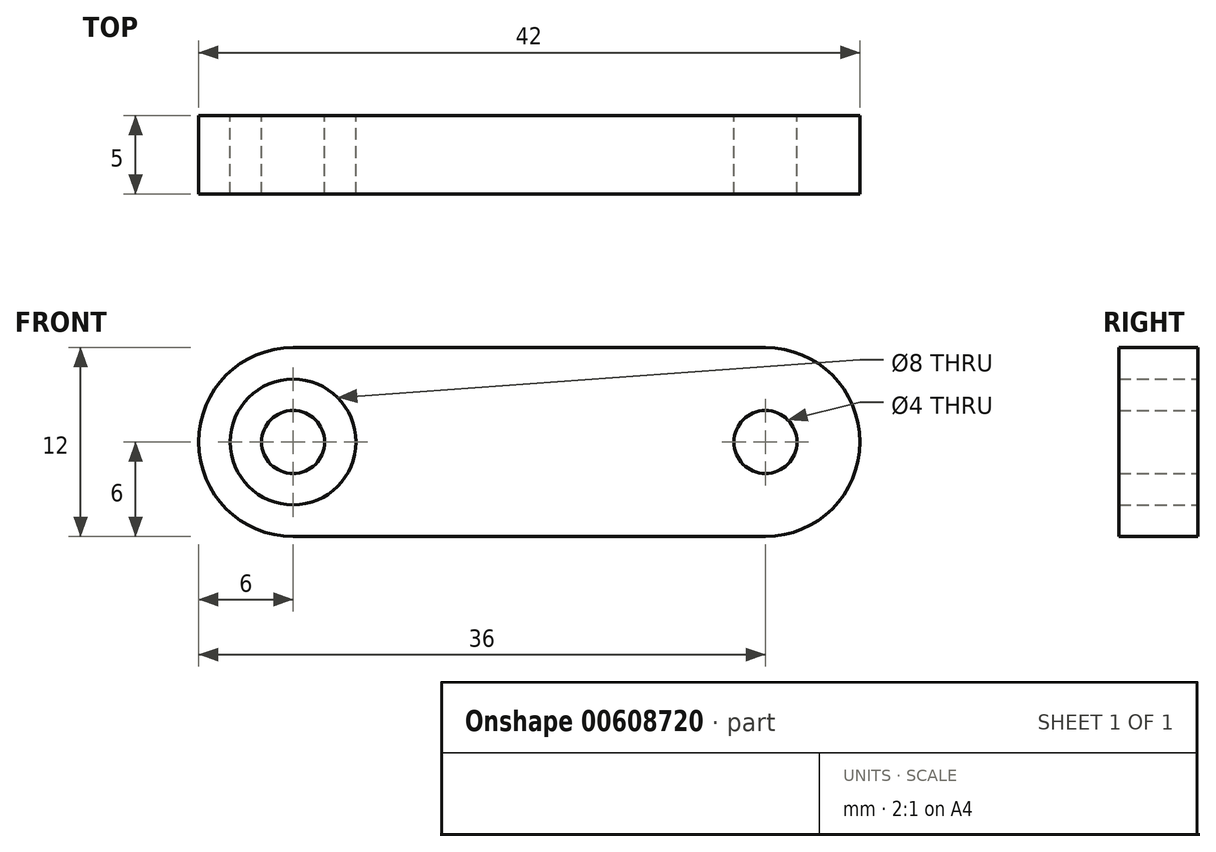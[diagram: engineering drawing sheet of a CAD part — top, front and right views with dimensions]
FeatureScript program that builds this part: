
annotation { "Feature Type Name" : "Feature", "Feature Type Description" : "" }
export const myFeature = defineFeature(function(context is Context, id is Id, definition is map)
    precondition{}
    {
        {
            var Q0;
            Q0=qCreatedBy(makeId("Front.planeOp"),FACE);
            var sketch = newSketch(context, id + "F0", { "sketchPlane" : qUnion([Q0])});
            skCircle(sketch, "E0", {"center": v(-15, 0) * mm, "radius": 2 * mm});
            skCircle(sketch, "E1", {"center": v(-15, 0) * mm, "radius": 4 * mm});
            skArc(sketch, "E2", {"start": v(-15, 6) * mm, "mid": v(-21, 0) * mm, "end": v(-15, -6) * mm});
            skLineSegment(sketch, "E3", {"start": v(-15, -6) * mm, "end": v(0, -6) * mm});
            skLineSegment(sketch, "E4", {"start": v(-15, 6) * mm, "end": v(0, 6) * mm});
            skLineSegment(sketch, "E5", {"start": v(0, 6) * mm, "end": v(0, -6) * mm, "construction": true});
            skCircle(sketch, "E6.MirrorC", {"center": v(15, 0) * mm, "radius": 2 * mm});
            skCircle(sketch, "E7.MirrorC", {"center": v(15, 0) * mm, "radius": 4 * mm});
            skLineSegment(sketch, "E8.MirrorCS", {"start": v(15, 6) * mm, "end": v(0, 6) * mm});
            skLineSegment(sketch, "E9.MirrorCS", {"start": v(15, -6) * mm, "end": v(0, -6) * mm});
            skArc(sketch, "E10.MirrorCS", {"start": v(15, 6) * mm, "mid": v(21, 0) * mm, "end": v(15, -6) * mm});
            skSolve(sketch);
        }
        {
            var Q0;
            Q0=makeQuery(id+"F0.imprint","IMPRINT",FACE,{"disambiguationData":[TD([[makeQuery(id+"F0.imprint","IMPRINT",EDGE,{"derivedFrom":sQuery(id+"F0.wireOp",EDGE,"E1")}),-1.0]])]});
            var Q1;
            Q1=makeQuery(id+"F0.imprint","IMPRINT",FACE,{"disambiguationData":[TD([[makeQuery(id+"F0.imprint","IMPRINT",EDGE,{"derivedFrom":sQuery(id+"F0.wireOp",EDGE,"E6.MirrorC")}),-1.0]])]});
            var Q2;
            Q2=makeQuery(id+"F0.imprint","IMPRINT",FACE,{"disambiguationData":[TD([[makeQuery(id+"F0.imprint","IMPRINT",EDGE,{"derivedFrom":sQuery(id+"F0.wireOp",EDGE,"E0")}),1.0]])]});
            extrude(context, id + "F1", {"entities" : qUnion([Q0, Q1, Q2]), "depth" : 5 * mm, "offsetDistance" : 25 * mm});
        }
    });
